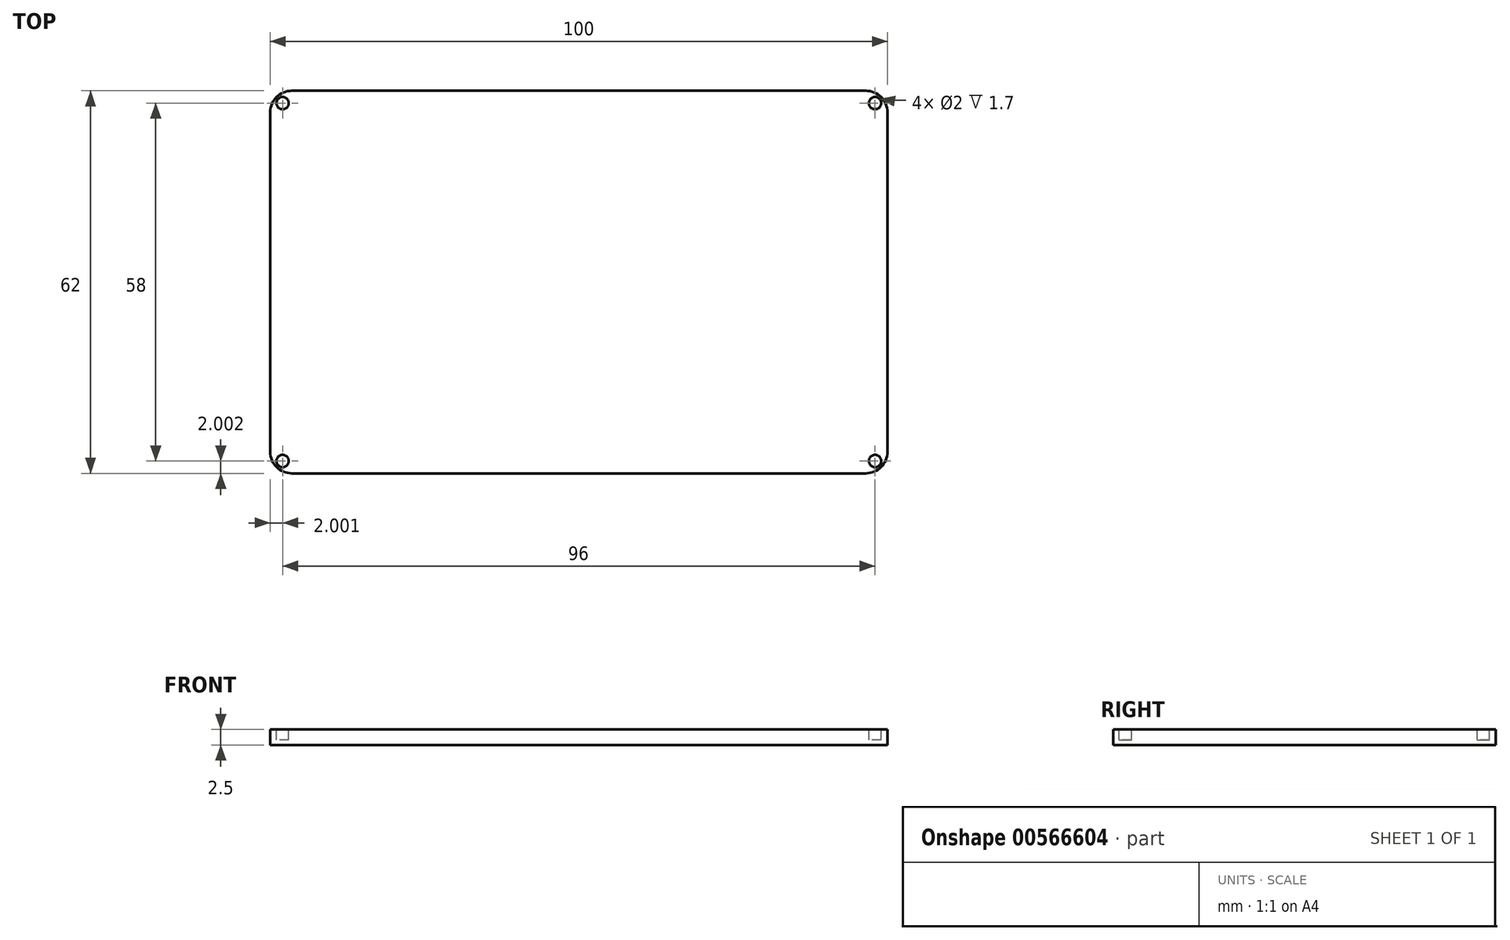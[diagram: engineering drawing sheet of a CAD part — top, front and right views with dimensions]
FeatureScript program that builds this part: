
annotation { "Feature Type Name" : "Feature", "Feature Type Description" : "" }
export const myFeature = defineFeature(function(context is Context, id is Id, definition is map)
    precondition{}
    {
        {
            var Q0;
            Q0=qCreatedBy(makeId("Top.planeOp"),FACE);
            var sketch = newSketch(context, id + "F0", { "sketchPlane" : qUnion([Q0])});
            skLineSegment(sketch, "E0", {"start": v(-42.28, 28.16) * mm, "end": v(57.72, 28.16) * mm});
            skLineSegment(sketch, "E1", {"start": v(57.72, 28.16) * mm, "end": v(57.72, -33.84) * mm});
            skLineSegment(sketch, "E2", {"start": v(57.72, -33.84) * mm, "end": v(-42.28, -33.84) * mm});
            skLineSegment(sketch, "E3", {"start": v(-42.28, -33.84) * mm, "end": v(-42.28, 28.16) * mm});
            skSolve(sketch);
        }
        {
            var Q0;
            Q0=makeQuery(id+"F0.imprint","IMPRINT",FACE,{"disambiguationData":[TD([[makeQuery(id+"F0.imprint","IMPRINT",EDGE,{"derivedFrom":sQuery(id+"F0.wireOp",EDGE,"E0")}),-1.0]])]});
            extrude(context, id + "F1", {"entities" : qUnion([Q0]), "depth" : 2.5 * mm, "offsetDistance" : 25 * mm});
        }
        {
            var Q0;
            Q0=makeQuery(id+"F1.opExtrude","SWEPT_EDGE",EDGE,{"disambiguationData":[OSD([sQuery(id+"F0.wireOp",EDGE,"E2"),sQuery(id+"F0.wireOp",EDGE,"E3")])]});
            var Q1;
            Q1=makeQuery(id+"F1.opExtrude","SWEPT_EDGE",EDGE,{"disambiguationData":[OSD([sQuery(id+"F0.wireOp",EDGE,"E0"),sQuery(id+"F0.wireOp",EDGE,"E3")])]});
            var Q2;
            Q2=makeQuery(id+"F1.opExtrude","SWEPT_EDGE",EDGE,{"disambiguationData":[OSD([sQuery(id+"F0.wireOp",EDGE,"E0"),sQuery(id+"F0.wireOp",EDGE,"E1")])]});
            var Q3;
            Q3=makeQuery(id+"F1.opExtrude","SWEPT_EDGE",EDGE,{"disambiguationData":[OSD([sQuery(id+"F0.wireOp",EDGE,"E1"),sQuery(id+"F0.wireOp",EDGE,"E2")])]});
            fillet(context, id + "F2", {"entities" : qUnion([Q0, Q1, Q2, Q3]), "radius" : 3.5 * mm, "tangentPropagation" : true, "allowEdgeOverflow" : false});
        }
        {
            var Q0;
            Q0=makeQuery(id+"F1.opExtrude","CAP_FACE",FACE,{"disambiguationData":[OSD([sQuery(id+"F0.wireOp",EDGE,"E0"),sQuery(id+"F0.wireOp",EDGE,"E1"),sQuery(id+"F0.wireOp",EDGE,"E2"),sQuery(id+"F0.wireOp",EDGE,"E3")])],"isStart":false});
            var sketch = newSketch(context, id + "F3", { "sketchPlane" : qUnion([Q0])});
            skLineSegment(sketch, "E4", {"start": v(0, 26.16) * mm, "end": v(-40.28, 26.16) * mm});
            skLineSegment(sketch, "E5", {"start": v(-40.28, 26.16) * mm, "end": v(-40.28, -31.84) * mm});
            skLineSegment(sketch, "E6", {"start": v(-40.28, -31.84) * mm, "end": v(55.72, -31.84) * mm});
            skLineSegment(sketch, "E7", {"start": v(55.72, -31.84) * mm, "end": v(55.72, 26.16) * mm});
            skLineSegment(sketch, "E8", {"start": v(55.72, 26.16) * mm, "end": v(0, 26.16) * mm});
            skPoint(sketch, "E9.start.orphan", {"position": v(0, 28.16) * mm});
            skPoint(sketch, "E10.end.orphan", {"position": v(-40.28, 3.96) * mm});
            skPoint(sketch, "E11.end.orphan", {"position": v(0, -31.84) * mm});
            skPoint(sketch, "E11.start.orphan", {"position": v(0, -33.84) * mm});
            skPoint(sketch, "E12.end.orphan", {"position": v(55.72, -14.5) * mm});
            skSolve(sketch);
        }
        {
            var Q0;
            Q0=makeQuery(id+"F1.opExtrude","CAP_FACE",FACE,{"disambiguationData":[OSD([sQuery(id+"F0.wireOp",EDGE,"E0"),sQuery(id+"F0.wireOp",EDGE,"E1"),sQuery(id+"F0.wireOp",EDGE,"E2"),sQuery(id+"F0.wireOp",EDGE,"E3")])],"isStart":false});
            var sketch = newSketch(context, id + "F4", { "sketchPlane" : qUnion([Q0])});
            skCircle(sketch, "E13", {"center": v(-40.28, 26.16) * mm, "radius": 1 * mm});
            skCircle(sketch, "E14", {"center": v(-40.28, -31.84) * mm, "radius": 1 * mm});
            skCircle(sketch, "E15", {"center": v(55.72, -31.84) * mm, "radius": 1 * mm});
            skCircle(sketch, "E16", {"center": v(55.72, 26.16) * mm, "radius": 1 * mm});
            skSolve(sketch);
        }
        {
            var Q0;
            Q0=makeQuery(id+"F4.imprint","IMPRINT",FACE,{"disambiguationData":[TD([[makeQuery(id+"F4.imprint","IMPRINT",EDGE,{"derivedFrom":sQuery(id+"F4.wireOp",EDGE,"E13")}),1.0]])]});
            var Q1;
            Q1=makeQuery(id+"F4.imprint","IMPRINT",FACE,{"disambiguationData":[TD([[makeQuery(id+"F4.imprint","IMPRINT",EDGE,{"derivedFrom":sQuery(id+"F4.wireOp",EDGE,"E14")}),1.0]])]});
            var Q2;
            Q2=makeQuery(id+"F4.imprint","IMPRINT",FACE,{"disambiguationData":[TD([[makeQuery(id+"F4.imprint","IMPRINT",EDGE,{"derivedFrom":sQuery(id+"F4.wireOp",EDGE,"E16")}),1.0]])]});
            var Q3;
            Q3=makeQuery(id+"F4.imprint","IMPRINT",FACE,{"disambiguationData":[TD([[makeQuery(id+"F4.imprint","IMPRINT",EDGE,{"derivedFrom":sQuery(id+"F4.wireOp",EDGE,"E15")}),1.0]])]});
            extrude(context, id + "F5", {"entities" : qUnion([Q0, Q1, Q2, Q3]), "operationType" : NewBodyOperationType.REMOVE, "oppositeDirection" : true, "depth" : 1.7 * mm, "offsetDistance" : 25 * mm});
        }
    });
